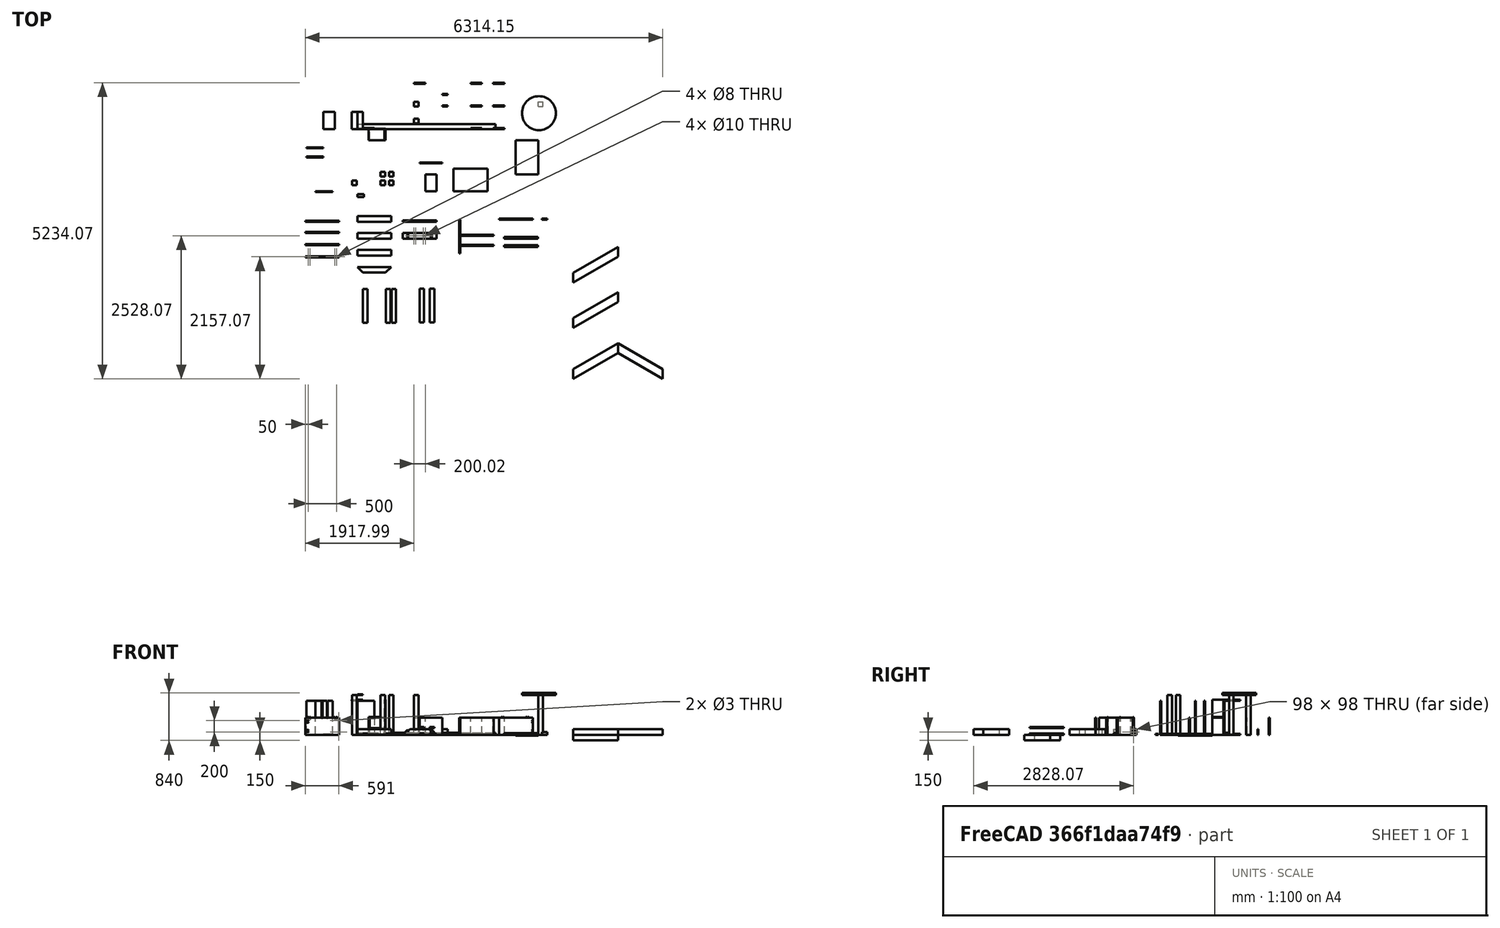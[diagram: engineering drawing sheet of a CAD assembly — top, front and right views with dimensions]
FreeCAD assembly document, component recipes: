
FREECAD ASSEMBLY — COMPONENT RECIPES ("Test001_features")

This assembly document has 25 components, labeled P0..P24 below (a component is one placed body or linked part). 18 of them carry a construction recipe — the FreeCAD feature program that regenerates the part from scratch, quoted from this document or its linked companion documents; the rest are supplied as boundary geometry only. No exploded tour is included for this assembly.
COMPONENT P0 — recipe-attached ("PDMirror Pad Body", modeled in this document).
Construction recipe (the document's own serialized feature program — sketch geometry with constraints, then the solid features built on it; lengths are millimeters unless a unit is written):

FEATURE [Sketcher::SketchObject] Sketch  label="Sketch001"
  AttachmentOffset = pos=(1300,-500,0) rot=(0,0,1;0rad)
  FullyConstrained = false
  MapMode = 5
  Placement = pos=(1300,-500,0) rot=(0,0,1;0rad)
  Support = -> [XY_Plane]
  sketch-geometry (4):
    g0: LineSegment StartX=0 StartY=-90.3636 StartZ=0 EndX=200 EndY=-90.3636 EndZ=0
    g1: LineSegment StartX=200 StartY=-90.3636 StartZ=0 EndX=200 EndY=-108.364 EndZ=0
    g2: LineSegment StartX=200 StartY=-108.364 StartZ=0 EndX=0 EndY=-108.364 EndZ=0
    g3: LineSegment StartX=0 StartY=-108.364 StartZ=0 EndX=0 EndY=-90.3636 EndZ=0
  constraints (11):
    c: Coincident(g0,g1)
    c: Coincident(g1,g2)
    c: Coincident(g2,g3)
    c: Coincident(g3,g0)
    c: Horizontal(g0)
    c: Horizontal(g2)
    c: Vertical(g1)
    c: Vertical(g3)
    c: DistanceX(g0,g0) = 200
    c: DistanceY(g3,g3) = 18
    c: DistanceX(g-1,g0) = 200
FEATURE [PartDesign::Pad] Pad  label="PDMirror Pad"
  AllowMultiFace = false
  Direction = (1,1,1)
  Length = 300
  Length2 = 100
  Profile = -> Sketch
  Type = 0
FEATURE [PartDesign::Mirrored] Mirrored
  BaseFeature = -> Pad
  MirrorPlane = -> Sketch [V_Axis]
  Originals = -> [Pad]
FEATURE [PartDesign::Body] Body  label="PDMirror Pad Body"
  Group = -> [Sketch,Pad,Mirrored]
  Origin = -> Origin
  Tip = -> Mirrored
COMPONENT P1 — recipe-attached ("Pad Single Body", modeled in this document).
Construction recipe (the document's own serialized feature program — sketch geometry with constraints, then the solid features built on it; lengths are millimeters unless a unit is written):

FEATURE [Sketcher::SketchObject] Sketch001  label="Sketch002"
  AttachmentOffset = pos=(1500,-1200,0) rot=(0,0,1;0rad)
  FullyConstrained = true
  MapMode = 5
  Placement = pos=(1500,-1200,0) rot=(0,0,1;0rad)
  Support = -> [XY_Plane001]
  sketch-geometry (4):
    g0: LineSegment StartX=-300 StartY=400 StartZ=0 EndX=-100 EndY=400 EndZ=0
    g1: LineSegment StartX=-100 StartY=400 StartZ=0 EndX=-100 EndY=100 EndZ=0
    g2: LineSegment StartX=-100 StartY=100 StartZ=0 EndX=-300 EndY=100 EndZ=0
    g3: LineSegment StartX=-300 StartY=100 StartZ=0 EndX=-300 EndY=400 EndZ=0
  constraints (12):
    c: Coincident(g0,g1)
    c: Coincident(g1,g2)
    c: Coincident(g2,g3)
    c: Coincident(g3,g0)
    c: Horizontal(g0)
    c: Horizontal(g2)
    c: Vertical(g1)
    c: Vertical(g3)
    c: DistanceX(g0,g0) = 200
    c: DistanceY(g3,g3) = 300
    c: DistanceY(g-1,g0) = 400
    c: DistanceX(g1,g-1) = 100
FEATURE [PartDesign::Pad] Pad001  label="Pad Single"
  AllowMultiFace = false
  Direction = (1,1,1)
  Length = 18
  Length2 = 100
  Profile = -> Sketch001
  Type = 0
FEATURE [PartDesign::Body] Body001  label="Pad Single Body"
  Group = -> [Sketch001,Pad001]
  Origin = -> Origin001
  Tip = -> Pad001
COMPONENT P2 — recipe-attached ("PDMulti 4 Pad Body", modeled in this document).
Construction recipe (the document's own serialized feature program — sketch geometry with constraints, then the solid features built on it; lengths are millimeters unless a unit is written):

FEATURE [Sketcher::SketchObject] Sketch002  label="Sketch003"
  AttachmentOffset = pos=(2000,-900,0) rot=(0,0,1;0rad)
  FullyConstrained = true
  MapMode = 5
  Placement = pos=(2000,-900,0) rot=(0,0,1;0rad)
  Support = -> [XY_Plane002]
  sketch-geometry (4):
    g0: LineSegment StartX=-300 StartY=200 StartZ=0 EndX=0 EndY=200 EndZ=0
    g1: LineSegment StartX=0 StartY=200 StartZ=0 EndX=0 EndY=0 EndZ=0
    g2: LineSegment StartX=0 StartY=0 StartZ=0 EndX=-300 EndY=0 EndZ=0
    g3: LineSegment StartX=-300 StartY=0 StartZ=0 EndX=-300 EndY=200 EndZ=0
  constraints (12):
    c: Coincident(g0,g1)
    c: Coincident(g1,g2)
    c: Coincident(g2,g3)
    c: Coincident(g3,g0)
    c: Horizontal(g0)
    c: Horizontal(g2)
    c: Vertical(g1)
    c: Vertical(g3)
    c: DistanceX(g0,g0) = 300
    c: DistanceY(g3,g3) = 200
    c: DistanceY(g1,g-1) = 0
    c: DistanceX(g1,g-1) = 0
FEATURE [PartDesign::Pad] Pad002  label="PDMulti 4 Pad"
  AllowMultiFace = false
  Direction = (1,1,1)
  Length = 18
  Length2 = 100
  Profile = -> Sketch002
  Type = 0
FEATURE [PartDesign::Mirrored] Mirrored001
  MirrorPlane = -> Sketch002 [V_Axis]
FEATURE [PartDesign::Mirrored] Mirrored002
  MirrorPlane = -> Sketch002 [H_Axis]
FEATURE [PartDesign::MultiTransform] MultiTransform
  BaseFeature = -> Pad002
  Originals = -> [Pad002]
  Transformations = -> [Mirrored001,Mirrored002]
FEATURE [PartDesign::Body] Body002  label="PDMulti 4 Pad Body"
  Group = -> [Sketch002,Pad002,MultiTransform,Mirrored001,Mirrored002]
  Origin = -> Origin002
  Tip = -> MultiTransform
COMPONENT P3 — recipe-attached ("PDMulti 8 Pad Body", modeled in this document).
Construction recipe (the document's own serialized feature program — sketch geometry with constraints, then the solid features built on it; lengths are millimeters unless a unit is written):

FEATURE [Sketcher::SketchObject] Sketch003  label="Sketch004"
  AttachmentOffset = pos=(3000,-500,0) rot=(0,0,1;0rad)
  FullyConstrained = true
  MapMode = 5
  Placement = pos=(3000,-500,0) rot=(0,0,1;0rad)
  Support = -> [XY_Plane003]
  sketch-geometry (4):
    g0: LineSegment StartX=-200 StartY=300 StartZ=0 EndX=0 EndY=300 EndZ=0
    g1: LineSegment StartX=0 StartY=300 StartZ=0 EndX=0 EndY=0 EndZ=0
    g2: LineSegment StartX=0 StartY=0 StartZ=0 EndX=-200 EndY=0 EndZ=0
    g3: LineSegment StartX=-200 StartY=0 StartZ=0 EndX=-200 EndY=300 EndZ=0
  constraints (11):
    c: Coincident(g0,g1)
    c: Coincident(g1,g2)
    c: Coincident(g2,g3)
    c: Coincident(g3,g0)
    c: Horizontal(g0)
    c: Horizontal(g2)
    c: Vertical(g1)
    c: Vertical(g3)
    c: Coincident(g1,g-1)
    c: DistanceX(g0,g0) = 200
    c: DistanceY(g3,g3) = 300
FEATURE [PartDesign::Pad] Pad003  label="PDMulti 8 Pad"
  AllowMultiFace = false
  Direction = (1,1,1)
  Length = 18
  Length2 = 100
  Profile = -> Sketch003
  Type = 0
FEATURE [PartDesign::Mirrored] Mirrored003
  MirrorPlane = -> Sketch003 [V_Axis]
FEATURE [PartDesign::Mirrored] Mirrored004
  MirrorPlane = -> Sketch003 [H_Axis]
FEATURE [PartDesign::Mirrored] Mirrored005
  MirrorPlane = -> XY_Plane003
FEATURE [PartDesign::MultiTransform] MultiTransform001
  BaseFeature = -> Pad003
  Originals = -> [Pad003]
  Transformations = -> [Mirrored003,Mirrored004,Mirrored005]
FEATURE [PartDesign::Body] Body003  label="PDMulti 8 Pad Body"
  Group = -> [Sketch003,Pad003,MultiTransform001,Mirrored003,Mirrored004,Mirrored005]
  Origin = -> Origin003
  Tip = -> MultiTransform001
COMPONENT P4 — recipe-attached ("Array Pad Body", modeled in this document).
Construction recipe (the document's own serialized feature program — sketch geometry with constraints, then the solid features built on it; lengths are millimeters unless a unit is written):

FEATURE [Sketcher::SketchObject] Sketch004  label="Sketch005"
  AttachmentOffset = pos=(500,-1000,0) rot=(0,0,1;0rad)
  FullyConstrained = true
  MapMode = 5
  Placement = pos=(500,-1000,0) rot=(0,0,1;0rad)
  Support = -> [XY_Plane004]
  sketch-geometry (4):
    g0: LineSegment StartX=-90 StartY=90 StartZ=0 EndX=-10 EndY=90 EndZ=0
    g1: LineSegment StartX=-10 StartY=90 StartZ=0 EndX=-10 EndY=10 EndZ=0
    g2: LineSegment StartX=-10 StartY=10 StartZ=0 EndX=-90 EndY=10 EndZ=0
    g3: LineSegment StartX=-90 StartY=10 StartZ=0 EndX=-90 EndY=90 EndZ=0
  constraints (12):
    c: Coincident(g0,g1)
    c: Coincident(g1,g2)
    c: Coincident(g2,g3)
    c: Coincident(g3,g0)
    c: Horizontal(g0)
    c: Horizontal(g2)
    c: Vertical(g1)
    c: Vertical(g3)
    c: DistanceY(g-1,g1) = 10
    c: DistanceX(g1,g-1) = 10
    c: DistanceX(g0,g0) = 80
    c: DistanceY(g3,g3) = 80
FEATURE [PartDesign::Pad] Pad004  label="Array Pad"
  AllowMultiFace = false
  Direction = (1,1,1)
  Length = 700
  Length2 = 100
  Profile = -> Sketch004
  Type = 0
FEATURE [PartDesign::Body] Body004  label="Array Pad Body"
  Group = -> [Sketch004,Pad004]
  Origin = -> Origin004
  Tip = -> Pad004
COMPONENT P5 — recipe-attached ("Array Polar Pad Body", modeled in this document).
Construction recipe (the document's own serialized feature program — sketch geometry with constraints, then the solid features built on it; lengths are millimeters unless a unit is written):

FEATURE [Sketcher::SketchObject] Sketch005  label="Sketch006"
  AttachmentOffset = pos=(0,-1000,0) rot=(0,0,1;0rad)
  FullyConstrained = true
  MapMode = 5
  Placement = pos=(0,-1000,0) rot=(0,0,1;0rad)
  Support = -> [XY_Plane005]
  sketch-geometry (4):
    g0: LineSegment StartX=-90 StartY=90 StartZ=0 EndX=-10 EndY=90 EndZ=0
    g1: LineSegment StartX=-10 StartY=90 StartZ=0 EndX=-10 EndY=10 EndZ=0
    g2: LineSegment StartX=-10 StartY=10 StartZ=0 EndX=-90 EndY=10 EndZ=0
    g3: LineSegment StartX=-90 StartY=10 StartZ=0 EndX=-90 EndY=90 EndZ=0
  constraints (12):
    c: Coincident(g0,g1)
    c: Coincident(g1,g2)
    c: Coincident(g2,g3)
    c: Coincident(g3,g0)
    c: Horizontal(g0)
    c: Horizontal(g2)
    c: Vertical(g1)
    c: Vertical(g3)
    c: DistanceY(g-1,g1) = 10
    c: DistanceX(g1,g-1) = 10
    c: DistanceX(g0,g0) = 80
    c: DistanceY(g3,g3) = 80
FEATURE [PartDesign::Pad] Pad005  label="Array Polar Pad"
  AllowMultiFace = false
  Direction = (1,1,1)
  Length = 700
  Length2 = 100
  Profile = -> Sketch005
  Type = 0
FEATURE [PartDesign::Body] Body005  label="Array Polar Pad Body"
  Group = -> [Sketch005,Pad005]
  Origin = -> Origin005
  Tip = -> Pad005
COMPONENT P6 — recipe-attached ("Table Top Parent Body", modeled in this document).
Construction recipe (the document's own serialized feature program — sketch geometry with constraints, then the solid features built on it; lengths are millimeters unless a unit is written):

FEATURE [Sketcher::SketchObject] Sketch006  label="Sketch007"
  AttachmentOffset = pos=(0,0,700) rot=(0,0,1;0rad)
  FullyConstrained = false
  MapMode = 5
  Placement = pos=(0,0,700) rot=(0,0,1;0rad)
  Support = -> [XY_Plane006]
  sketch-geometry (1):
    g0: Circle CenterX=3208.45 CenterY=279.77 CenterZ=0 NormalX=0 NormalY=0 NormalZ=1 AngleXU=0 Radius=300
  constraints (1):
    c: Radius(g0) = 300  'This is my round table top radius'
FEATURE [PartDesign::Pad] Pad006  label="Table Top"
  Direction = (1,1,1)
  Length = 40
  Length2 = 100
  Profile = -> Sketch006
  Type = 0
FEATURE [PartDesign::Body] Body006  label="Table Top Parent Body"
  Group = -> [Sketch006,Pad006]
  Origin = -> Origin006
  Tip = -> Pad006
COMPONENT P7 — recipe-attached ("Screw, Body", modeled in this document).
Construction recipe (the document's own serialized feature program — sketch geometry with constraints, then the solid features built on it; lengths are millimeters unless a unit is written):

FEATURE [Sketcher::SketchObject] Sketch007  label="Core, Pattern"
  FullyConstrained = true
  MapMode = 5
  Placement = pos=(0,0,0) rot=(1,0,0;1.5708rad)
  Support = -> [XZ_Plane007]
  expr: Constraints[10] = Spreadsheet.corer
  expr: Constraints[11] = 2 * Spreadsheet.tjump
  expr: Constraints[12] = Spreadsheet.sheight
  expr: Constraints[13] = Spreadsheet.hheight1
  expr: Constraints[14] = Spreadsheet.hheight2
  expr: Constraints[15] = Spreadsheet.hr
  expr: Constraints[16] = Spreadsheet.hheight1
  sketch-geometry (6):
    g0: LineSegment StartX=0 StartY=0 StartZ=0 EndX=1.5 EndY=3.8 EndZ=0
    g1: LineSegment StartX=1.5 StartY=3.8 StartZ=0 EndX=1.5 EndY=37 EndZ=0
    g2: LineSegment StartX=1.5 StartY=37 StartZ=0 EndX=2 EndY=37.5 EndZ=0
    g3: LineSegment StartX=2 StartY=37.5 StartZ=0 EndX=3.87 EndY=40 EndZ=0
    g4: LineSegment StartX=3.87 StartY=40 StartZ=0 EndX=0 EndY=40 EndZ=0
    g5: LineSegment StartX=0 StartY=40 StartZ=0 EndX=0 EndY=0 EndZ=0
  constraints (17):
    c: Coincident(g-1,g0)
    c: Coincident(g0,g1)
    c: Vertical(g1)
    c: Coincident(g1,g2)
    c: Coincident(g2,g3)
    c: Coincident(g3,g4)
    c: PointOnObject(g4,g-2)
    c: Horizontal(g4)
    c: Coincident(g4,g5)
    c: Coincident(g5,g0)
    c: DistanceX(g0,g0) = 1.5
    c: DistanceY(g0,g0) = 3.8
    c: DistanceY(g5,g5) = 40
    c: DistanceY(g1,g2) = 0.5
    c: DistanceY(g2,g3) = 2.5
    c: DistanceX(g4,g3) = 3.87
    c: DistanceX(g1,g2) = 0.5
FEATURE [PartDesign::Revolution] Revolution  label="Core"
  Angle = 360
  Axis = (0,-2e-16,1)
  Base = (0,0,0)
  Placement = pos=(0,0,0) rot=(1,0,0;1.5708rad)
  Profile = -> Sketch007
  ReferenceAxis = -> Sketch007 [V_Axis]
  Reversed = true
FEATURE [Sketcher::SketchObject] Sketch008  label="Thread, Pattern"
  FullyConstrained = true
  MapMode = 5
  Placement = pos=(0,0,0) rot=(1,0,0;1.5708rad)
  Support = -> [XZ_Plane007]
  expr: Constraints[2] = Spreadsheet.spikesize
  expr: Constraints[3] = Spreadsheet.corer
  sketch-geometry (3):
    g0: LineSegment StartX=1.5 StartY=3.675 StartZ=0 EndX=2 EndY=3.8 EndZ=0
    g1: LineSegment StartX=2 StartY=3.8 StartZ=0 EndX=1.5 EndY=3.925 EndZ=0
    g2: LineSegment StartX=1.5 StartY=3.925 StartZ=0 EndX=1.5 EndY=3.675 EndZ=0
  constraints (9):
    c: Coincident(g0,g1)
    c: Equal(g0,g1)
    c: DistanceY(g-1,g0) = 3.8
    c: DistanceX(g-1,g0) = 1.5
    c: DistanceX(g0,g0) = 0.5
    c: DistanceY(g0,g1) = 0.25
    c: Vertical(g1,g0)
    c: Coincident(g2,g1)
    c: Coincident(g2,g0)
FEATURE [PartDesign::AdditiveHelix] AdditiveHelix  label="Thread, Core"
  Angle = 0
  Axis = (0,-2e-16,1)
  Base = (0,0,0)
  BaseFeature = -> Revolution
  Growth = 0
  HasBeenEdited = true
  Height = 20.4
  LeftHanded = false
  Mode = 0
  Outside = false
  Pitch = 1.9
  Placement = pos=(0,0,0) rot=(1,0,0;1.5708rad)
  Profile = -> Sketch008
  ReferenceAxis = -> Sketch008 [V_Axis]
  Turns = 10.7368
  expr: Height = Spreadsheet.theight - Spreadsheet.spikesize
  expr: Pitch = Spreadsheet.tjump
FEATURE [PartDesign::AdditiveHelix] AdditiveHelix001  label="Thread, Spike"
  Angle = -30
  Axis = (0,-2e-16,1)
  Base = (0,0,0)
  BaseFeature = -> AdditiveHelix
  Growth = -1.09697
  HasBeenEdited = true
  Height = 2.53333
  LeftHanded = false
  Mode = 0
  Outside = false
  Pitch = 1.9
  Placement = pos=(0,0,0) rot=(1,0,0;1.5708rad)
  Profile = -> Sketch008
  ReferenceAxis = -> Sketch008 [V_Axis]
  Reversed = true
  Turns = 1.33333
  expr: Height = 2 * Spreadsheet.spikesize / 3
  expr: Pitch = Spreadsheet.tjump
FEATURE [Sketcher::SketchObject] Sketch009  label="Bit, Pattern 1"
  FullyConstrained = true
  MapMode = 5
  Placement = pos=(0,0,0) rot=(0.57735,0.57735,0.57735;2.0944rad)
  Support = -> [YZ_Plane007]
  expr: Constraints[16] = Spreadsheet.hheight2 / 4
  expr: Constraints[6] = Spreadsheet.coredia
  expr: Constraints[7] = Spreadsheet.sheight
  expr: Constraints[8] = Spreadsheet.bitsize
  expr: Constraints[9] = Spreadsheet.hheight2 / 2
  sketch-geometry (6):
    g0: LineSegment StartX=-2.13 StartY=40 StartZ=0 EndX=2.13 EndY=40 EndZ=0
    g1: LineSegment StartX=2.13 StartY=40 StartZ=0 EndX=1.5 EndY=38.75 EndZ=0
    g2: LineSegment StartX=1.5 StartY=38.75 StartZ=0 EndX=0.875 EndY=38.75 EndZ=0
    g3: LineSegment StartX=-1.5 StartY=38.75 StartZ=0 EndX=-2.13 EndY=40 EndZ=0
    g4: ArcOfCircle CenterX=0 CenterY=40 CenterZ=0 NormalX=0 NormalY=0 NormalZ=1 AngleXU=0 Radius=1.52582 StartAngle=4.10166 EndAngle=5.32311
    g5: LineSegment StartX=-0.875 StartY=38.75 StartZ=0 EndX=-1.5 EndY=38.75 EndZ=0
  constraints (17):
    c: Coincident(g0,g1)
    c: Coincident(g1,g2)
    c: Coincident(g5,g3)
    c: Coincident(g3,g0)
    c: Symmetric(g1,g5,g-2)
    c: Symmetric(g0,g0,g-2)
    c: DistanceX(g5,g2) = 3
    c: DistanceY(g-1,g0) = 40
    c: DistanceX(g0,g0) = 4.26
    c: DistanceY(g1,g0) = 1.25
    c: Horizontal(g4,g0)
    c: PointOnObject(g4,g-2)
    c: Coincident(g2,g4)
    c: Coincident(g5,g4)
    c: Horizontal(g3,g4)
    c: Horizontal(g4,g2)
    c: DistanceX(g2,g1) = 0.625
FEATURE [PartDesign::Pocket] Pocket  label="Bit, Pocket 1"
  BaseFeature = -> AdditiveHelix001
  Direction = (-1,2e-16,-3e-16)
  Length = 1
  Length2 = 5
  Midplane = true
  Placement = pos=(0,0,0) rot=(1,0,0;1.5708rad)
  Profile = -> Sketch009
  ReferenceAxis = -> Sketch009 [N_Axis]
  Type = 0
FEATURE [Sketcher::SketchObject] Sketch010  label="Bit, Line, Pattern 1"
  AttachmentOffset = pos=(0,0,0) rot=(0,1,0;0.785398rad)
  FullyConstrained = true
  MapMode = 5
  Placement = pos=(0,0,0) rot=(0.281085,0.678598,0.678598;2.59356rad)
  Support = -> [YZ_Plane007]
  expr: Constraints[10] = Spreadsheet.sheight
  expr: Constraints[6] = Spreadsheet.bitsize
  sketch-geometry (4):
    g0: LineSegment StartX=2.13 StartY=40 StartZ=0 EndX=2.13 EndY=39.9 EndZ=0
    g1: LineSegment StartX=2.13 StartY=39.9 StartZ=0 EndX=-2.13 EndY=39.9 EndZ=0
    g2: LineSegment StartX=-2.13 StartY=39.9 StartZ=0 EndX=-2.13 EndY=40 EndZ=0
    g3: LineSegment StartX=-2.13 StartY=40 StartZ=0 EndX=2.13 EndY=40 EndZ=0
  constraints (11):
    c: Coincident(g0,g1)
    c: Coincident(g1,g2)
    c: Coincident(g3,g2)
    c: Coincident(g3,g0)
    c: Equal(g1,g3)
    c: Equal(g0,g2)
    c: DistanceX(g3,g3) = 4.26
    c: Vertical(g2)
    c: Symmetric(g1,g0,g-2)
    c: DistanceY(g0,g0) = 0.1
    c: DistanceY(g-1,g0) = 40
FEATURE [PartDesign::Pocket] Pocket001  label="Bit, Lines 1"
  BaseFeature = -> Pocket
  Direction = (-0.707107,-0.707107,1e-16)
  Length = 0.1
  Length2 = 5
  Midplane = true
  Placement = pos=(0,0,0) rot=(1,0,0;1.5708rad)
  Profile = -> Sketch010
  ReferenceAxis = -> Sketch010 [N_Axis]
  Type = 0
FEATURE [PartDesign::PolarPattern] PolarPattern  label="Bit, PolarPattern"
  Angle = 90
  Axis = -> Sketch010 [V_Axis]
  BaseFeature = -> Pocket001
  Occurrences = 2
  Originals = -> [Pocket001,Pocket]
  Placement = pos=(0,0,0) rot=(1,0,0;1.5708rad)
FEATURE [Sketcher::SketchObject] Sketch011  label="Thread, Top, Pattern"
  FullyConstrained = true
  MapMode = 5
  Placement = pos=(0,0,0) rot=(1,0,0;1.5708rad)
  Support = -> [XZ_Plane007]
  expr: Constraints[2] = Spreadsheet.tjump
  expr: Constraints[4] = Spreadsheet.corer
  expr: Constraints[5] = Spreadsheet.theight
  sketch-geometry (4):
    g0: LineSegment StartX=1.5 StartY=26.1 StartZ=0 EndX=1.5 EndY=24.2 EndZ=0
    g1: LineSegment StartX=1.5 StartY=24.2 StartZ=0 EndX=2.5 EndY=24.2 EndZ=0
    g2: LineSegment StartX=1.5 StartY=26.1 StartZ=0 EndX=2.5 EndY=26.1 EndZ=0
    g3: LineSegment StartX=2.5 StartY=26.1 StartZ=0 EndX=2.5 EndY=24.2 EndZ=0
  constraints (12):
    c: Vertical(g0)
    c: Coincident(g0,g1)
    c: DistanceY(g0,g0) = 1.9
    c: DistanceX(g0,g1) = 1
    c: DistanceX(g-1,g0) = 1.5
    c: DistanceY(g-1,g1) = 24.2
    c: Coincident(g0,g2)
    c: Coincident(g2,g3)
    c: Coincident(g3,g1)
    c: Horizontal(g2)
    c: Vertical(g3)
    c: Horizontal(g1)
FEATURE [PartDesign::SubtractiveHelix] SubtractiveHelix  label="Thread, Top"
  Angle = 15
  Axis = (0,-2e-16,1)
  Base = (0,0,0)
  BaseFeature = -> PolarPattern
  Growth = 0.509103
  HasBeenEdited = true
  Height = 1.9
  LeftHanded = false
  Mode = 0
  Outside = false
  Pitch = 1.9
  Placement = pos=(0,0,0) rot=(1,0,0;1.5708rad)
  Profile = -> Sketch011
  ReferenceAxis = -> Sketch011 [V_Axis]
  Reversed = true
  Turns = 1
  expr: Height = Spreadsheet.tjump
  expr: Pitch = Spreadsheet.tjump
FEATURE [PartDesign::Body] Body007  label="Screw, Body"
  Group = -> [Sketch007,Revolution,Sketch008,AdditiveHelix,AdditiveHelix001,Sketch009,Pocket,Sketch010,Pocket001,PolarPattern,Sketch011,SubtractiveHelix]
  Origin = -> Origin007
  Tip = -> SubtractiveHelix
COMPONENT P8 — geometry summary ("Link"; no construction recipe available for this part):
  bounding box: 600.0 x 300.0 x 180.0 mm
  tessellated surface: 24 triangles
  volume: 6480000 mm^3 (20% of its bounding box)
  symmetry: 2-fold rotationally symmetric about the x axis; 2-fold rotationally symmetric about the y axis; 2-fold rotationally symmetric about the z axis; mirror-symmetric across its x mid-plane, y mid-plane, z mid-plane
COMPONENT P9 — geometry summary ("Link, Cut"; no construction recipe available for this part):
  bounding box: 600.0 x 300.0 x 18.0 mm
  tessellated surface: 44 triangles
  volume: 3037824 mm^3 (94% of its bounding box)
  symmetry: mirror-symmetric across its y mid-plane
COMPONENT P10 — geometry summary ("Link, nested 1 link "; no construction recipe available for this part):
  bounding box: 600.0 x 180.0 x 20.0 mm
  tessellated surface: 24 triangles
  volume: 1920000 mm^3 (89% of its bounding box)
  symmetry: 2-fold rotationally symmetric about the x axis; 2-fold rotationally symmetric about the y axis; 2-fold rotationally symmetric about the z axis; mirror-symmetric across its x mid-plane, y mid-plane, z mid-plane
COMPONENT P11 — geometry summary ("Link, nested 2 link"; no construction recipe available for this part):
  bounding box: 600.0 x 180.0 x 20.0 mm
  tessellated surface: 24 triangles
  volume: 1920000 mm^3 (89% of its bounding box)
  symmetry: 2-fold rotationally symmetric about the x axis; 2-fold rotationally symmetric about the y axis; 2-fold rotationally symmetric about the z axis; mirror-symmetric across its x mid-plane, y mid-plane, z mid-plane
COMPONENT P12 — recipe-attached ("Link, panelZX002 ", modeled in this document).
Construction recipe (the document's own serialized feature program — sketch geometry with constraints, then the solid features built on it; lengths are millimeters unless a unit is written):

FEATURE [Sketcher::SketchObject] Sketch035  label="Pattern, panel2pad001"
  FullyConstrained = true
  MapMode = 5
  Placement = pos=(0,0,0) rot=(1,0,0;1.5708rad)
  Support = -> [XZ_Plane025]
  sketch-geometry (4):
    g0: LineSegment StartX=0 StartY=600 StartZ=0 EndX=300 EndY=600 EndZ=0
    g1: LineSegment StartX=300 StartY=600 StartZ=0 EndX=300 EndY=0 EndZ=0
    g2: LineSegment StartX=300 StartY=0 StartZ=0 EndX=0 EndY=0 EndZ=0
    g3: LineSegment StartX=0 StartY=0 StartZ=0 EndX=0 EndY=600 EndZ=0
  constraints (11):
    c: Coincident(g0,g1)
    c: Coincident(g1,g2)
    c: Coincident(g2,g3)
    c: Coincident(g3,g0)
    c: Horizontal(g0)
    c: Horizontal(g2)
    c: Vertical(g1)
    c: Vertical(g3)
    c: Coincident(g2,g-1)
    c: DistanceX(g0,g0) = 300  'SizeX'
    c: DistanceY(g3,g3) = 600  'SizeY'
FEATURE [PartDesign::Pad] Pad015  label="panel2pad"
  Direction = (0,-1,2e-16)
  Length = 18
  Length2 = 10
  Placement = pos=(0,0,0) rot=(1,0,0;1.5708rad)
  Profile = -> Sketch035
  Reversed = true
  Type = 0
FEATURE [Sketcher::SketchObject] routerPattern002
  FullyConstrained = true
  Placement = pos=(150,1.332e-13,600) rot=(0,1,0;1.5708rad)
  sketch-geometry (4):
    g0: ArcOfCircle CenterX=18 CenterY=-18 CenterZ=0 NormalX=0 NormalY=0 NormalZ=1 AngleXU=0 Radius=18 StartAngle=1.5708 EndAngle=3.14159
    g1: ArcOfCircle CenterX=-18 CenterY=18 CenterZ=0 NormalX=0 NormalY=0 NormalZ=1 AngleXU=0 Radius=18 StartAngle=4.71239 EndAngle=6.28319
    g2: ArcOfCircle CenterX=18 CenterY=18 CenterZ=0 NormalX=0 NormalY=0 NormalZ=1 AngleXU=0 Radius=18 StartAngle=3.14159 EndAngle=4.71239
    g3: ArcOfCircle CenterX=-18 CenterY=-18 CenterZ=0 NormalX=0 NormalY=0 NormalZ=1 AngleXU=0 Radius=18 StartAngle=6.28318 EndAngle=7.85398
  constraints (16):
    c: Equal(g3,g1)
    c: Equal(g1,g2)
    c: Equal(g2,g0)
    c: Vertical(g0,g2)
    c: Horizontal(g3,g0)
    c: Vertical(g1,g3)
    c: Horizontal(g1,g2)
    c: Coincident(g1,g2)
    c: Coincident(g0,g2)
    c: Coincident(g3,g0)
    c: Coincident(g3,g1)
    c: PointOnObject(g1,g-1)
    c: PointOnObject(g1,g-2)
    c: DistanceY(g0,g-1) = 18
    c: Vertical(g0,g0)
    c: Horizontal(g1,g1)
FEATURE [PartDesign::Pocket] router002  label="RoundOver "
  BaseFeature = -> Pad015
  Direction = (-1,0,-2e-16)
  Length = 5
  Length2 = 5
  Midplane = true
  Placement = pos=(0,0,0) rot=(1,0,0;1.5708rad)
  Profile = -> routerPattern002
  Type = 1
FEATURE [Sketcher::SketchObject] routerPattern003
  FullyConstrained = true
  Placement = pos=(300,6.7e-14,300) rot=(0,0,1;0rad)
  sketch-geometry (4):
    g0: ArcOfCircle CenterX=18 CenterY=-18 CenterZ=0 NormalX=0 NormalY=0 NormalZ=1 AngleXU=0 Radius=18 StartAngle=1.5708 EndAngle=3.14159
    g1: ArcOfCircle CenterX=-18 CenterY=18 CenterZ=0 NormalX=0 NormalY=0 NormalZ=1 AngleXU=0 Radius=18 StartAngle=4.71239 EndAngle=6.28319
    g2: ArcOfCircle CenterX=18 CenterY=18 CenterZ=0 NormalX=0 NormalY=0 NormalZ=1 AngleXU=0 Radius=18 StartAngle=3.14159 EndAngle=4.71239
    g3: ArcOfCircle CenterX=-18 CenterY=-18 CenterZ=0 NormalX=0 NormalY=0 NormalZ=1 AngleXU=0 Radius=18 StartAngle=6.28318 EndAngle=7.85398
  constraints (16):
    c: Equal(g3,g1)
    c: Equal(g1,g2)
    c: Equal(g2,g0)
    c: Vertical(g0,g2)
    c: Horizontal(g3,g0)
    c: Vertical(g1,g3)
    c: Horizontal(g1,g2)
    c: Coincident(g1,g2)
    c: Coincident(g0,g2)
    c: Coincident(g3,g0)
    c: Coincident(g3,g1)
    c: PointOnObject(g1,g-1)
    c: PointOnObject(g1,g-2)
    c: DistanceY(g0,g-1) = 18
    c: Vertical(g0,g0)
    c: Horizontal(g1,g1)
FEATURE [PartDesign::Pocket] router003  label="RoundOver 001"
  BaseFeature = -> router002
  Direction = (0,0,-1)
  Length = 5
  Length2 = 5
  Midplane = true
  Placement = pos=(0,0,0) rot=(1,0,0;1.5708rad)
  Profile = -> routerPattern003
  Type = 1
FEATURE [Sketcher::SketchObject] routerPattern004
  FullyConstrained = true
  Placement = pos=(150,0,0) rot=(0,1,0;1.5708rad)
  sketch-geometry (4):
    g0: ArcOfCircle CenterX=18 CenterY=-18 CenterZ=0 NormalX=0 NormalY=0 NormalZ=1 AngleXU=0 Radius=18 StartAngle=1.5708 EndAngle=3.14159
    g1: ArcOfCircle CenterX=-18 CenterY=18 CenterZ=0 NormalX=0 NormalY=0 NormalZ=1 AngleXU=0 Radius=18 StartAngle=4.71239 EndAngle=6.28319
    g2: ArcOfCircle CenterX=18 CenterY=18 CenterZ=0 NormalX=0 NormalY=0 NormalZ=1 AngleXU=0 Radius=18 StartAngle=3.14159 EndAngle=4.71239
    g3: ArcOfCircle CenterX=-18 CenterY=-18 CenterZ=0 NormalX=0 NormalY=0 NormalZ=1 AngleXU=0 Radius=18 StartAngle=1.97117e-06 EndAngle=1.5708
  constraints (16):
    c: Equal(g3,g1)
    c: Equal(g1,g2)
    c: Equal(g2,g0)
    c: Vertical(g0,g2)
    c: Horizontal(g3,g0)
    c: Vertical(g1,g3)
    c: Horizontal(g1,g2)
    c: Coincident(g1,g2)
    c: Coincident(g0,g2)
    c: Coincident(g3,g0)
    c: Coincident(g3,g1)
    c: PointOnObject(g1,g-1)
    c: PointOnObject(g1,g-2)
    c: DistanceY(g0,g-1) = 18
    c: Vertical(g0,g0)
    c: Horizontal(g1,g1)
FEATURE [PartDesign::Pocket] router004  label="RoundOver 002"
  BaseFeature = -> router003
  Direction = (-1,0,-2e-16)
  Length = 5
  Length2 = 5
  Midplane = true
  Placement = pos=(0,0,0) rot=(1,0,0;1.5708rad)
  Profile = -> routerPattern004
  Type = 1
FEATURE [Sketcher::SketchObject] routerPattern005
  FullyConstrained = true
  Placement = pos=(0,6.7e-14,300) rot=(0,0,1;0rad)
  sketch-geometry (4):
    g0: ArcOfCircle CenterX=18 CenterY=-18 CenterZ=0 NormalX=0 NormalY=0 NormalZ=1 AngleXU=0 Radius=18 StartAngle=1.5708 EndAngle=3.14159
    g1: ArcOfCircle CenterX=-18 CenterY=18 CenterZ=0 NormalX=0 NormalY=0 NormalZ=1 AngleXU=0 Radius=18 StartAngle=4.71239 EndAngle=6.28319
    g2: ArcOfCircle CenterX=18 CenterY=18 CenterZ=0 NormalX=0 NormalY=0 NormalZ=1 AngleXU=0 Radius=18 StartAngle=3.14159 EndAngle=4.71239
    g3: ArcOfCircle CenterX=-18 CenterY=-18 CenterZ=0 NormalX=0 NormalY=0 NormalZ=1 AngleXU=0 Radius=18 StartAngle=6.28318 EndAngle=7.85398
  constraints (16):
    c: Equal(g3,g1)
    c: Equal(g1,g2)
    c: Equal(g2,g0)
    c: Vertical(g0,g2)
    c: Horizontal(g3,g0)
    c: Vertical(g1,g3)
    c: Horizontal(g1,g2)
    c: Coincident(g1,g2)
    c: Coincident(g0,g2)
    c: Coincident(g3,g0)
    c: Coincident(g3,g1)
    c: PointOnObject(g1,g-1)
    c: PointOnObject(g1,g-2)
    c: DistanceY(g0,g-1) = 18
    c: Vertical(g0,g0)
    c: Horizontal(g1,g1)
FEATURE [PartDesign::Pocket] router005  label="RoundOver 003"
  BaseFeature = -> router004
  Direction = (0,0,-1)
  Length = 5
  Length2 = 5
  Midplane = true
  Placement = pos=(0,0,0) rot=(1,0,0;1.5708rad)
  Profile = -> routerPattern005
  Type = 1
FEATURE [PartDesign::Body] Body016  label="Body, panel2pad001"
  Group = -> [Sketch035,Pad015,routerPattern002,router002,routerPattern003,router003,routerPattern004,router004,routerPattern005,router005]
  Origin = -> Origin025
  Tip = -> router005
COMPONENT P13 — same part as P12; its construction recipe is shown at P12.
COMPONENT P14 — geometry summary ("Link, Screw 4 x 40 mm "; no construction recipe available for this part):
  bounding box: 40.0 x 7.7 x 7.4 mm
  tessellated surface: 492 triangles
  volume: 317 mm^3 (14% of its bounding box)
COMPONENT P15 — geometry summary ("Link, Screw 4 x 40 mm 001"; no construction recipe available for this part):
  bounding box: 40.0 x 7.7 x 7.4 mm
  tessellated surface: 492 triangles
  volume: 317 mm^3 (14% of its bounding box)
COMPONENT P16 — recipe-attached ("Part, Construction", modeled in this document).
Construction recipe (the document's own serialized feature program — sketch geometry with constraints, then the solid features built on it; lengths are millimeters unless a unit is written):

FEATURE [Sketcher::SketchObject] Sketch012  label="Pattern, Construction"
  AttachmentOffset = pos=(0,-1638,0) rot=(0,0,1;0rad)
  FullyConstrained = true
  MapMode = 5
  Placement = pos=(0,-1638,0) rot=(0,0,1;0rad)
  Support = -> [XY_Plane009]
  sketch-geometry (4):
    g0: LineSegment StartX=0 StartY=100 StartZ=0 EndX=600 EndY=100 EndZ=0
    g1: LineSegment StartX=600 StartY=100 StartZ=0 EndX=600 EndY=0 EndZ=0
    g2: LineSegment StartX=600 StartY=0 StartZ=0 EndX=0 EndY=0 EndZ=0
    g3: LineSegment StartX=0 StartY=0 StartZ=0 EndX=0 EndY=100 EndZ=0
  constraints (11):
    c: Coincident(g0,g1)
    c: Coincident(g1,g2)
    c: Coincident(g2,g3)
    c: Coincident(g3,g0)
    c: Horizontal(g0)
    c: Horizontal(g2)
    c: Vertical(g1)
    c: Vertical(g3)
    c: Coincident(g2,g-1)
    c: DistanceX(g0,g0) = 600  'SizeX'
    c: DistanceY(g3,g3) = 100  'SizeY'
FEATURE [PartDesign::Pad] Pad007  label="Profile Simple"
  Direction = (0,0,1)
  Length = 100
  Length2 = 10
  Profile = -> Sketch012
  Type = 0
FEATURE [PartDesign::Thickness] Profile
  Base = -> Pad007 [Face2,Face4]
  BaseFeature = -> Pad007
  Intersection = false
  Join = 0
  Mode = 0
  Reversed = true
  SupportTransform = false
  Value = 1
FEATURE [PartDesign::Body] Body008  label="Body, Construction"
  Group = -> [Sketch012,Pad007,Profile]
  Origin = -> Origin009
  Tip = -> Profile
COMPONENT P17 — recipe-attached ("Part, Construction001", modeled in this document).
Construction recipe (the document's own serialized feature program — sketch geometry with constraints, then the solid features built on it; lengths are millimeters unless a unit is written):

FEATURE [Sketcher::SketchObject] Sketch013  label="Pattern, Construction001"
  AttachmentOffset = pos=(0,-1938,0) rot=(0,0,1;0rad)
  FullyConstrained = true
  MapMode = 5
  Placement = pos=(0,-1938,0) rot=(0,0,1;0rad)
  Support = -> [XY_Plane011]
  sketch-geometry (4):
    g0: LineSegment StartX=0 StartY=100 StartZ=0 EndX=600 EndY=100 EndZ=0
    g1: LineSegment StartX=600 StartY=100 StartZ=0 EndX=600 EndY=0 EndZ=0
    g2: LineSegment StartX=600 StartY=0 StartZ=0 EndX=0 EndY=0 EndZ=0
    g3: LineSegment StartX=0 StartY=0 StartZ=0 EndX=0 EndY=100 EndZ=0
  constraints (11):
    c: Coincident(g0,g1)
    c: Coincident(g1,g2)
    c: Coincident(g2,g3)
    c: Coincident(g3,g0)
    c: Horizontal(g0)
    c: Horizontal(g2)
    c: Vertical(g1)
    c: Vertical(g3)
    c: Coincident(g2,g-1)
    c: DistanceX(g0,g0) = 600  'SizeX'
    c: DistanceY(g3,g3) = 100  'SizeY'
FEATURE [PartDesign::Pad] Pad008  label="Profile Angle 1"
  Direction = (0,0,1)
  Length = 100
  Length2 = 10
  Profile = -> Sketch013
  Type = 0
FEATURE [PartDesign::Thickness] Angle
  Base = -> Pad008 [Face2,Face4,Face6]
  BaseFeature = -> Pad008
  Intersection = false
  Join = 0
  Mode = 0
  Reversed = true
  SupportTransform = false
  Value = 1
FEATURE [PartDesign::Body] Body009  label="Body, Construction001"
  Group = -> [Sketch013,Pad008,Angle]
  Origin = -> Origin011
  Tip = -> Angle
COMPONENT P18 — recipe-attached ("Part, Construction002", modeled in this document).
Construction recipe (the document's own serialized feature program — sketch geometry with constraints, then the solid features built on it; lengths are millimeters unless a unit is written):

FEATURE [Sketcher::SketchObject] Sketch014  label="Pattern, Construction002"
  AttachmentOffset = pos=(0,-2238,0) rot=(0,0,1;0rad)
  FullyConstrained = true
  MapMode = 5
  Placement = pos=(0,-2238,0) rot=(0,0,1;0rad)
  Support = -> [XY_Plane013]
  sketch-geometry (4):
    g0: LineSegment StartX=0 StartY=100 StartZ=0 EndX=600 EndY=100 EndZ=0
    g1: LineSegment StartX=600 StartY=100 StartZ=0 EndX=600 EndY=0 EndZ=0
    g2: LineSegment StartX=600 StartY=0 StartZ=0 EndX=0 EndY=0 EndZ=0
    g3: LineSegment StartX=0 StartY=0 StartZ=0 EndX=0 EndY=100 EndZ=0
  constraints (11):
    c: Coincident(g0,g1)
    c: Coincident(g1,g2)
    c: Coincident(g2,g3)
    c: Coincident(g3,g0)
    c: Horizontal(g0)
    c: Horizontal(g2)
    c: Vertical(g1)
    c: Vertical(g3)
    c: Coincident(g2,g-1)
    c: DistanceX(g0,g0) = 600  'SizeX'
    c: DistanceY(g3,g3) = 100  'SizeY'
FEATURE [PartDesign::Pad] Pad009  label="Profile Angle 2"
  Direction = (0,0,1)
  Length = 100
  Length2 = 10
  Profile = -> Sketch014
  Type = 0
FEATURE [PartDesign::Thickness] Angle001
  Base = -> Pad009 [Face2,Face4,Face3,Face6]
  BaseFeature = -> Pad009
  Intersection = false
  Join = 0
  Mode = 0
  Reversed = true
  SupportTransform = false
  Value = 1
FEATURE [PartDesign::Body] Body010  label="Body, Construction002"
  Group = -> [Sketch014,Pad009,Angle001]
  Origin = -> Origin013
  Tip = -> Angle001
COMPONENT P19 — recipe-attached ("Part, Construction003", modeled in this document).
Construction recipe (the document's own serialized feature program — sketch geometry with constraints, then the solid features built on it; lengths are millimeters unless a unit is written):

FEATURE [Sketcher::SketchObject] Sketch015  label="Pattern, Construction003"
  AttachmentOffset = pos=(0,-2538,0) rot=(0,0,1;0rad)
  FullyConstrained = true
  MapMode = 5
  Placement = pos=(0,-2538,0) rot=(0,0,1;0rad)
  Support = -> [XY_Plane015]
  sketch-geometry (4):
    g0: LineSegment StartX=0 StartY=100 StartZ=0 EndX=600 EndY=100 EndZ=0
    g1: LineSegment StartX=600 StartY=100 StartZ=0 EndX=600 EndY=0 EndZ=0
    g2: LineSegment StartX=600 StartY=0 StartZ=0 EndX=0 EndY=0 EndZ=0
    g3: LineSegment StartX=0 StartY=0 StartZ=0 EndX=0 EndY=100 EndZ=0
  constraints (11):
    c: Coincident(g0,g1)
    c: Coincident(g1,g2)
    c: Coincident(g2,g3)
    c: Coincident(g3,g0)
    c: Horizontal(g0)
    c: Horizontal(g2)
    c: Vertical(g1)
    c: Vertical(g3)
    c: Coincident(g2,g-1)
    c: DistanceX(g0,g0) = 600  'SizeX'
    c: DistanceY(g3,g3) = 100  'SizeY'
FEATURE [PartDesign::Pad] Pad010  label="Profile Angle 45 Cut"
  Direction = (0,0,1)
  Length = 100
  Length2 = 10
  Profile = -> Sketch015
  Type = 0
FEATURE [PartDesign::Thickness] Angle002
  Base = -> Pad010 [Face2,Face4,Face3,Face6]
  BaseFeature = -> Pad010
  Intersection = false
  Join = 0
  Mode = 0
  Reversed = true
  SupportTransform = false
  Value = 1
FEATURE [PartDesign::Chamfer] Angle45Cut
  Angle = 45
  Base = -> Angle002 [Edge11,Edge13]
  BaseFeature = -> Angle002
  ChamferType = 0
  FlipDirection = false
  Size = 98.99
  Size2 = 1
  SupportTransform = false
  UseAllEdges = false
FEATURE [PartDesign::Body] Body011  label="Body, Construction003"
  Group = -> [Sketch015,Pad010,Angle002,Angle45Cut]
  Origin = -> Origin015
  Tip = -> Angle45Cut
COMPONENT P20 — recipe-attached ("Part, Frame", modeled in this document).
Construction recipe (the document's own serialized feature program — sketch geometry with constraints, then the solid features built on it; lengths are millimeters unless a unit is written):

FEATURE [Sketcher::SketchObject] Sketch016  label="Pattern, Frame"
  AttachmentOffset = pos=(800,0,1618) rot=(0,0,1;0rad)
  FullyConstrained = true
  MapMode = 5
  Placement = pos=(800,-1618,-3.593e-13) rot=(1,0,0;1.5708rad)
  Support = -> [XZ_Plane017]
  sketch-geometry (4):
    g0: LineSegment StartX=0 StartY=40 StartZ=0 EndX=600 EndY=40 EndZ=0
    g1: LineSegment StartX=600 StartY=40 StartZ=0 EndX=600 EndY=0 EndZ=0
    g2: LineSegment StartX=600 StartY=0 StartZ=0 EndX=0 EndY=0 EndZ=0
    g3: LineSegment StartX=0 StartY=0 StartZ=0 EndX=0 EndY=40 EndZ=0
  constraints (11):
    c: Coincident(g0,g1)
    c: Coincident(g1,g2)
    c: Coincident(g2,g3)
    c: Coincident(g3,g0)
    c: Horizontal(g0)
    c: Horizontal(g2)
    c: Vertical(g1)
    c: Vertical(g3)
    c: Coincident(g2,g-1)
    c: DistanceX(g0,g0) = 600  'SizeX'
    c: DistanceY(g3,g3) = 40  'SizeY'
FEATURE [PartDesign::Pad] Pad011  label="Frame"
  Direction = (0,-1,2e-16)
  Length = 20
  Length2 = 10
  Placement = pos=(0,0,0) rot=(1,0,0;1.5708rad)
  Profile = -> Sketch016
  Type = 0
FEATURE [PartDesign::Chamfer] Frame45Cut
  Angle = 45
  Base = -> Pad011 [Edge1,Edge2]
  BaseFeature = -> Pad011
  ChamferType = 0
  FlipDirection = false
  Placement = pos=(0,0,0) rot=(1,0,0;1.5708rad)
  Size = 39.99
  Size2 = 1
  SupportTransform = false
  UseAllEdges = false
FEATURE [PartDesign::Body] Body012  label="Body, Frame"
  Group = -> [Sketch016,Pad011,Frame45Cut]
  Origin = -> Origin017
  Tip = -> Frame45Cut
COMPONENT P21 — recipe-attached ("Part, Frame001", modeled in this document).
Construction recipe (the document's own serialized feature program — sketch geometry with constraints, then the solid features built on it; lengths are millimeters unless a unit is written):

FEATURE [Sketcher::SketchObject] Sketch017  label="Pattern, Frame001"
  AttachmentOffset = pos=(800,-1938,0) rot=(0,0,1;0rad)
  FullyConstrained = true
  MapMode = 5
  Placement = pos=(800,-1938,0) rot=(0,0,1;0rad)
  Support = -> [XY_Plane019]
  sketch-geometry (4):
    g0: LineSegment StartX=0 StartY=100 StartZ=0 EndX=600 EndY=100 EndZ=0
    g1: LineSegment StartX=600 StartY=100 StartZ=0 EndX=600 EndY=0 EndZ=0
    g2: LineSegment StartX=600 StartY=0 StartZ=0 EndX=0 EndY=0 EndZ=0
    g3: LineSegment StartX=0 StartY=0 StartZ=0 EndX=0 EndY=100 EndZ=0
  constraints (11):
    c: Coincident(g0,g1)
    c: Coincident(g1,g2)
    c: Coincident(g2,g3)
    c: Coincident(g3,g0)
    c: Horizontal(g0)
    c: Horizontal(g2)
    c: Vertical(g1)
    c: Vertical(g3)
    c: Coincident(g2,g-1)
    c: DistanceX(g0,g0) = 600  'SizeX'
    c: DistanceY(g3,g3) = 100  'SizeY'
FEATURE [PartDesign::Pad] Pad012  label="Frame Table Foot"
  Direction = (0,0,1)
  Length = 100
  Length2 = 10
  Profile = -> Sketch017
  Type = 0
FEATURE [PartDesign::Chamfer] Frame45Cut001
  Angle = 45
  Base = -> Pad012 [Edge12,Edge7]
  BaseFeature = -> Pad012
  ChamferType = 0
  FlipDirection = false
  Size = 99.99
  Size2 = 1
  SupportTransform = false
  UseAllEdges = false
FEATURE [Sketcher::SketchObject] routerPattern
  FullyConstrained = true
  Placement = pos=(1300.01,-1888,100) rot=(1,0,0;1.5708rad)
  sketch-geometry (4):
    g0: ArcOfCircle CenterX=49.9999 CenterY=-49.9999 CenterZ=0 NormalX=0 NormalY=0 NormalZ=1 AngleXU=0 Radius=49.9999 StartAngle=1.5708 EndAngle=3.14159
    g1: ArcOfCircle CenterX=-49.9999 CenterY=49.9999 CenterZ=0 NormalX=0 NormalY=0 NormalZ=1 AngleXU=0 Radius=49.9999 StartAngle=4.71239 EndAngle=6.28319
    g2: ArcOfCircle CenterX=49.9999 CenterY=49.9999 CenterZ=0 NormalX=0 NormalY=0 NormalZ=1 AngleXU=0 Radius=49.9999 StartAngle=3.14159 EndAngle=4.71239
    g3: ArcOfCircle CenterX=-49.9999 CenterY=-49.9999 CenterZ=0 NormalX=0 NormalY=0 NormalZ=1 AngleXU=0 Radius=49.9999 StartAngle=6.28318 EndAngle=7.85398
  constraints (16):
    c: Equal(g3,g1)
    c: Equal(g1,g2)
    c: Equal(g2,g0)
    c: Vertical(g0,g2)
    c: Horizontal(g3,g0)
    c: Vertical(g1,g3)
    c: Horizontal(g1,g2)
    c: Coincident(g1,g2)
    c: Coincident(g0,g2)
    c: Coincident(g3,g0)
    c: Coincident(g3,g1)
    c: PointOnObject(g1,g-1)
    c: PointOnObject(g1,g-2)
    c: DistanceY(g0,g-1) = 50
    c: Vertical(g0,g0)
    c: Horizontal(g1,g1)
FEATURE [PartDesign::Pocket] router  label="RoundOver2 "
  BaseFeature = -> Frame45Cut001
  Direction = (0,1,-2e-16)
  Length = 5
  Length2 = 5
  Midplane = true
  Profile = -> routerPattern
  Type = 1
FEATURE [Sketcher::SketchObject] routerPattern001
  FullyConstrained = true
  Placement = pos=(899.99,-1888,100) rot=(1,0,0;1.5708rad)
  sketch-geometry (4):
    g0: ArcOfCircle CenterX=50 CenterY=-50 CenterZ=0 NormalX=0 NormalY=0 NormalZ=1 AngleXU=0 Radius=50 StartAngle=1.5708 EndAngle=3.14159
    g1: ArcOfCircle CenterX=-50 CenterY=50 CenterZ=0 NormalX=0 NormalY=0 NormalZ=1 AngleXU=0 Radius=50 StartAngle=4.71239 EndAngle=6.28319
    g2: ArcOfCircle CenterX=50 CenterY=50 CenterZ=0 NormalX=0 NormalY=0 NormalZ=1 AngleXU=0 Radius=50 StartAngle=3.14159 EndAngle=4.71239
    g3: ArcOfCircle CenterX=-50 CenterY=-50 CenterZ=0 NormalX=0 NormalY=0 NormalZ=1 AngleXU=0 Radius=50 StartAngle=6.28318 EndAngle=7.85398
  constraints (16):
    c: Equal(g3,g1)
    c: Equal(g1,g2)
    c: Equal(g2,g0)
    c: Vertical(g0,g2)
    c: Horizontal(g3,g0)
    c: Vertical(g1,g3)
    c: Horizontal(g1,g2)
    c: Coincident(g1,g2)
    c: Coincident(g0,g2)
    c: Coincident(g3,g0)
    c: Coincident(g3,g1)
    c: PointOnObject(g1,g-1)
    c: PointOnObject(g1,g-2)
    c: DistanceY(g0,g-1) = 50
    c: Vertical(g0,g0)
    c: Horizontal(g1,g1)
FEATURE [PartDesign::Pocket] router001  label="RoundOver2 001"
  BaseFeature = -> router
  Direction = (0,1,-2e-16)
  Length = 5
  Length2 = 5
  Midplane = true
  Profile = -> routerPattern001
  Type = 1
FEATURE [Sketcher::SketchObject] Sketch018
  FullyConstrained = true
  MapMode = 5
  Placement = pos=(1200.01,-1888,100) rot=(0,0,1;0rad)
  sketch-geometry (1):
    g0: Circle CenterX=0 CenterY=0 CenterZ=0 NormalX=0 NormalY=0 NormalZ=1 AngleXU=0 Radius=5
  constraints (2):
    c: Coincident(g0,g-1)
    c: Diameter(g0) = 10  'Hole00Diameter'
FEATURE [PartDesign::Hole] Hole
  BaseFeature = -> router001
  CustomThreadClearance = 0
  Depth = 25
  DepthType = 0
  Diameter = 10
  DrillForDepth = true
  DrillPoint = 1
  DrillPointAngle = 118
  HoleCutCountersinkAngle = 90
  HoleCutCustomValues = false
  HoleCutDepth = 25
  HoleCutDiameter = 10
  HoleCutType = 0
  ModelThread = false
  Profile = -> Sketch018
  Tapered = false
  TaperedAngle = 90
  ThreadClass = 0
  ThreadDepth = 25
  ThreadDepthType = 0
  ThreadDirection = 0
  ThreadFit = 0
  ThreadSize = 0
  ThreadType = 0
  Threaded = false
  UseCustomThreadClearance = false
FEATURE [Sketcher::SketchObject] Sketch019
  FullyConstrained = true
  MapMode = 5
  Placement = pos=(1168.01,-1888,100) rot=(0,0,1;0rad)
  sketch-geometry (1):
    g0: Circle CenterX=0 CenterY=0 CenterZ=0 NormalX=0 NormalY=0 NormalZ=1 AngleXU=0 Radius=5
  constraints (2):
    c: Coincident(g0,g-1)
    c: Diameter(g0) = 10  'Hole00Diameter'
FEATURE [PartDesign::Hole] Hole001
  BaseFeature = -> Hole
  CustomThreadClearance = 0
  Depth = 25
  DepthType = 0
  Diameter = 10
  DrillForDepth = true
  DrillPoint = 1
  DrillPointAngle = 118
  HoleCutCountersinkAngle = 90
  HoleCutCustomValues = false
  HoleCutDepth = 25
  HoleCutDiameter = 10
  HoleCutType = 0
  ModelThread = false
  Profile = -> Sketch019
  Tapered = false
  TaperedAngle = 90
  ThreadClass = 0
  ThreadDepth = 25
  ThreadDepthType = 0
  ThreadDirection = 0
  ThreadFit = 0
  ThreadSize = 0
  ThreadType = 0
  Threaded = false
  UseCustomThreadClearance = false
FEATURE [Sketcher::SketchObject] Sketch020
  FullyConstrained = true
  MapMode = 5
  Placement = pos=(999.99,-1888,100) rot=(0,0,1;0rad)
  sketch-geometry (1):
    g0: Circle CenterX=0 CenterY=0 CenterZ=0 NormalX=0 NormalY=0 NormalZ=1 AngleXU=0 Radius=5
  constraints (2):
    c: Coincident(g0,g-1)
    c: Diameter(g0) = 10  'Hole00Diameter'
FEATURE [PartDesign::Hole] Hole002
  BaseFeature = -> Hole001
  CustomThreadClearance = 0
  Depth = 25
  DepthType = 0
  Diameter = 10
  DrillForDepth = true
  DrillPoint = 1
  DrillPointAngle = 118
  HoleCutCountersinkAngle = 90
  HoleCutCustomValues = false
  HoleCutDepth = 25
  HoleCutDiameter = 10
  HoleCutType = 0
  ModelThread = false
  Profile = -> Sketch020
  Tapered = false
  TaperedAngle = 90
  ThreadClass = 0
  ThreadDepth = 25
  ThreadDepthType = 0
  ThreadDirection = 0
  ThreadFit = 0
  ThreadSize = 0
  ThreadType = 0
  Threaded = false
  UseCustomThreadClearance = false
FEATURE [Sketcher::SketchObject] Sketch021
  FullyConstrained = true
  MapMode = 5
  Placement = pos=(1031.99,-1888,100) rot=(0,0,1;0rad)
  sketch-geometry (1):
    g0: Circle CenterX=0 CenterY=0 CenterZ=0 NormalX=0 NormalY=0 NormalZ=1 AngleXU=0 Radius=5
  constraints (2):
    c: Coincident(g0,g-1)
    c: Diameter(g0) = 10  'Hole00Diameter'
FEATURE [PartDesign::Hole] Hole003
  BaseFeature = -> Hole002
  CustomThreadClearance = 0
  Depth = 25
  DepthType = 0
  Diameter = 10
  DrillForDepth = true
  DrillPoint = 1
  DrillPointAngle = 118
  HoleCutCountersinkAngle = 90
  HoleCutCustomValues = false
  HoleCutDepth = 25
  HoleCutDiameter = 10
  HoleCutType = 0
  ModelThread = false
  Profile = -> Sketch021
  Tapered = false
  TaperedAngle = 90
  ThreadClass = 0
  ThreadDepth = 25
  ThreadDepthType = 0
  ThreadDirection = 0
  ThreadFit = 0
  ThreadSize = 0
  ThreadType = 0
  Threaded = false
  UseCustomThreadClearance = false
FEATURE [PartDesign::Body] Body013  label="Body, Frame001"
  Group = -> [Sketch017,Pad012,Frame45Cut001,routerPattern,router,routerPattern001,router001,Sketch018,Hole,Sketch019,Hole001,Sketch020,Hole002,Sketch021,Hole003]
  Origin = -> Origin019
  Tip = -> Hole003
COMPONENT P22 — recipe-attached ("Part, Holes", modeled in this document).
Construction recipe (the document's own serialized feature program — sketch geometry with constraints, then the solid features built on it; lengths are millimeters unless a unit is written):

FEATURE [Sketcher::SketchObject] Sketch022  label="Pattern, panel with dowels"
  AttachmentOffset = pos=(-918,0,2250) rot=(0,0,1;0rad)
  FullyConstrained = true
  MapMode = 5
  Placement = pos=(-918,-2250,-4.996e-13) rot=(1,0,0;1.5708rad)
  Support = -> [XZ_Plane021]
  sketch-geometry (4):
    g0: LineSegment StartX=0 StartY=300 StartZ=0 EndX=600 EndY=300 EndZ=0
    g1: LineSegment StartX=600 StartY=300 StartZ=0 EndX=600 EndY=0 EndZ=0
    g2: LineSegment StartX=600 StartY=0 StartZ=0 EndX=0 EndY=0 EndZ=0
    g3: LineSegment StartX=0 StartY=0 StartZ=0 EndX=0 EndY=300 EndZ=0
  constraints (11):
    c: Coincident(g0,g1)
    c: Coincident(g1,g2)
    c: Coincident(g2,g3)
    c: Coincident(g3,g0)
    c: Horizontal(g0)
    c: Horizontal(g2)
    c: Vertical(g1)
    c: Vertical(g3)
    c: Coincident(g2,g-1)
    c: DistanceX(g0,g0) = 600  'SizeX'
    c: DistanceY(g3,g3) = 300  'SizeY'
FEATURE [PartDesign::Pad] Pad013  label="panel with holes"
  Direction = (0,-1,2e-16)
  Length = 18
  Length2 = 10
  Placement = pos=(0,0,0) rot=(1,0,0;1.5708rad)
  Profile = -> Sketch022
  Type = 0
FEATURE [Sketcher::SketchObject] Sketch023
  FullyConstrained = true
  MapMode = 5
  Placement = pos=(-368,-2259,300) rot=(0,0,1;0rad)
  sketch-geometry (1):
    g0: Circle CenterX=0 CenterY=0 CenterZ=0 NormalX=0 NormalY=0 NormalZ=1 AngleXU=0 Radius=4
  constraints (2):
    c: Coincident(g0,g-1)
    c: Diameter(g0) = 8  'Hole00Diameter'
FEATURE [PartDesign::Hole] Hole004
  BaseFeature = -> Pad013
  CustomThreadClearance = 0
  Depth = 35
  DepthType = 0
  Diameter = 8
  DrillForDepth = true
  DrillPoint = 1
  DrillPointAngle = 118
  HoleCutCountersinkAngle = 90
  HoleCutCustomValues = false
  HoleCutDepth = 35
  HoleCutDiameter = 8
  HoleCutType = 0
  ModelThread = false
  Placement = pos=(0,0,0) rot=(1,0,0;1.5708rad)
  Profile = -> Sketch023
  Tapered = false
  TaperedAngle = 90
  ThreadClass = 0
  ThreadDepth = 35
  ThreadDepthType = 0
  ThreadDirection = 0
  ThreadFit = 0
  ThreadSize = 0
  ThreadType = 0
  Threaded = false
  UseCustomThreadClearance = false
FEATURE [Sketcher::SketchObject] Sketch024
  FullyConstrained = true
  MapMode = 5
  Placement = pos=(-400,-2259,300) rot=(0,0,1;0rad)
  sketch-geometry (1):
    g0: Circle CenterX=0 CenterY=0 CenterZ=0 NormalX=0 NormalY=0 NormalZ=1 AngleXU=0 Radius=4
  constraints (2):
    c: Coincident(g0,g-1)
    c: Diameter(g0) = 8  'Hole00Diameter'
FEATURE [PartDesign::Hole] Hole005
  BaseFeature = -> Hole004
  CustomThreadClearance = 0
  Depth = 35
  DepthType = 0
  Diameter = 8
  DrillForDepth = true
  DrillPoint = 1
  DrillPointAngle = 118
  HoleCutCountersinkAngle = 90
  HoleCutCustomValues = false
  HoleCutDepth = 35
  HoleCutDiameter = 8
  HoleCutType = 0
  ModelThread = false
  Placement = pos=(0,0,0) rot=(1,0,0;1.5708rad)
  Profile = -> Sketch024
  Tapered = false
  TaperedAngle = 90
  ThreadClass = 0
  ThreadDepth = 35
  ThreadDepthType = 0
  ThreadDirection = 0
  ThreadFit = 0
  ThreadSize = 0
  ThreadType = 0
  Threaded = false
  UseCustomThreadClearance = false
FEATURE [Sketcher::SketchObject] Sketch025
  FullyConstrained = true
  MapMode = 5
  Placement = pos=(-868,-2259,300) rot=(0,0,1;0rad)
  sketch-geometry (1):
    g0: Circle CenterX=0 CenterY=0 CenterZ=0 NormalX=0 NormalY=0 NormalZ=1 AngleXU=0 Radius=4
  constraints (2):
    c: Coincident(g0,g-1)
    c: Diameter(g0) = 8  'Hole00Diameter'
FEATURE [PartDesign::Hole] Hole006
  BaseFeature = -> Hole005
  CustomThreadClearance = 0
  Depth = 35
  DepthType = 0
  Diameter = 8
  DrillForDepth = true
  DrillPoint = 1
  DrillPointAngle = 118
  HoleCutCountersinkAngle = 90
  HoleCutCustomValues = false
  HoleCutDepth = 35
  HoleCutDiameter = 8
  HoleCutType = 0
  ModelThread = false
  Placement = pos=(0,0,0) rot=(1,0,0;1.5708rad)
  Profile = -> Sketch025
  Tapered = false
  TaperedAngle = 90
  ThreadClass = 0
  ThreadDepth = 35
  ThreadDepthType = 0
  ThreadDirection = 0
  ThreadFit = 0
  ThreadSize = 0
  ThreadType = 0
  Threaded = false
  UseCustomThreadClearance = false
FEATURE [Sketcher::SketchObject] Sketch026
  FullyConstrained = true
  MapMode = 5
  Placement = pos=(-836,-2259,300) rot=(0,0,1;0rad)
  sketch-geometry (1):
    g0: Circle CenterX=0 CenterY=0 CenterZ=0 NormalX=0 NormalY=0 NormalZ=1 AngleXU=0 Radius=4
  constraints (2):
    c: Coincident(g0,g-1)
    c: Diameter(g0) = 8  'Hole00Diameter'
FEATURE [PartDesign::Hole] Hole007
  BaseFeature = -> Hole006
  CustomThreadClearance = 0
  Depth = 35
  DepthType = 0
  Diameter = 8
  DrillForDepth = true
  DrillPoint = 1
  DrillPointAngle = 118
  HoleCutCountersinkAngle = 90
  HoleCutCustomValues = false
  HoleCutDepth = 35
  HoleCutDiameter = 8
  HoleCutType = 0
  ModelThread = false
  Placement = pos=(0,0,0) rot=(1,0,0;1.5708rad)
  Profile = -> Sketch026
  Tapered = false
  TaperedAngle = 90
  ThreadClass = 0
  ThreadDepth = 35
  ThreadDepthType = 0
  ThreadDirection = 0
  ThreadFit = 0
  ThreadSize = 0
  ThreadType = 0
  Threaded = false
  UseCustomThreadClearance = false
FEATURE [Sketcher::SketchObject] Sketch027
  FullyConstrained = true
  MapMode = 5
  Placement = pos=(-327,-2268,250) rot=(1,0,0;1.5708rad)
  sketch-geometry (2):
    g0: Circle CenterX=0 CenterY=0 CenterZ=0 NormalX=0 NormalY=0 NormalZ=1 AngleXU=0 Radius=1.5
    g1: Circle CenterX=0 CenterY=0 CenterZ=0 NormalX=0 NormalY=0 NormalZ=1 AngleXU=0 Radius=5
  constraints (4):
    c: Coincident(g0,g-1)
    c: Diameter(g0) = 3  'Hole00Diameter'
    c: Coincident(g1,g-1)
    c: Diameter(g1) = 10  'Countersink00Diameter'
FEATURE [PartDesign::Hole] Countersink
  BaseFeature = -> Hole007
  CustomThreadClearance = 0
  Depth = 40
  DepthType = 0
  Diameter = 3
  DrillForDepth = true
  DrillPoint = 1
  DrillPointAngle = 118
  HoleCutCountersinkAngle = 90
  HoleCutCustomValues = false
  HoleCutDepth = 5
  HoleCutDiameter = 10
  HoleCutType = 2
  ModelThread = false
  Placement = pos=(0,0,0) rot=(1,0,0;1.5708rad)
  Profile = -> Sketch027
  Tapered = false
  TaperedAngle = 90
  ThreadClass = 0
  ThreadDepth = 40
  ThreadDepthType = 0
  ThreadDirection = 0
  ThreadFit = 0
  ThreadSize = 0
  ThreadType = 0
  Threaded = false
  UseCustomThreadClearance = false
FEATURE [Sketcher::SketchObject] Sketch028
  FullyConstrained = true
  MapMode = 5
  Placement = pos=(-327,-2268,50) rot=(1,0,0;1.5708rad)
  sketch-geometry (2):
    g0: Circle CenterX=0 CenterY=0 CenterZ=0 NormalX=0 NormalY=0 NormalZ=1 AngleXU=0 Radius=1.5
    g1: Circle CenterX=0 CenterY=0 CenterZ=0 NormalX=0 NormalY=0 NormalZ=1 AngleXU=0 Radius=5
  constraints (4):
    c: Coincident(g0,g-1)
    c: Diameter(g0) = 3  'Hole00Diameter'
    c: Coincident(g1,g-1)
    c: Diameter(g1) = 10  'Countersink00Diameter'
FEATURE [PartDesign::Hole] Countersink001
  BaseFeature = -> Countersink
  CustomThreadClearance = 0
  Depth = 40
  DepthType = 0
  Diameter = 3
  DrillForDepth = true
  DrillPoint = 1
  DrillPointAngle = 118
  HoleCutCountersinkAngle = 90
  HoleCutCustomValues = false
  HoleCutDepth = 5
  HoleCutDiameter = 10
  HoleCutType = 2
  ModelThread = false
  Placement = pos=(0,0,0) rot=(1,0,0;1.5708rad)
  Profile = -> Sketch028
  Tapered = false
  TaperedAngle = 90
  ThreadClass = 0
  ThreadDepth = 40
  ThreadDepthType = 0
  ThreadDirection = 0
  ThreadFit = 0
  ThreadSize = 0
  ThreadType = 0
  Threaded = false
  UseCustomThreadClearance = false
FEATURE [Sketcher::SketchObject] Sketch029
  FullyConstrained = true
  MapMode = 5
  Placement = pos=(-858,-2274,250) rot=(0.677661,0.519988,0.519988;1.95044rad)
  sketch-geometry (2):
    g0: Circle CenterX=0 CenterY=0 CenterZ=0 NormalX=0 NormalY=0 NormalZ=1 AngleXU=0 Radius=1.5
    g1: Circle CenterX=0 CenterY=0 CenterZ=0 NormalX=0 NormalY=0 NormalZ=1 AngleXU=0 Radius=4.75
  constraints (4):
    c: Coincident(g0,g-1)
    c: Diameter(g0) = 3  'Tip0hole00Diameter'
    c: Coincident(g1,g-1)
    c: Diameter(g1) = 9.5  'Pocket0hole00Diameter'
FEATURE [PartDesign::Hole] PocketHole
  BaseFeature = -> Countersink001
  CustomThreadClearance = 0
  Depth = 90
  DepthType = 0
  Diameter = 3
  DrillForDepth = false
  DrillPoint = 0
  DrillPointAngle = 118
  HoleCutCountersinkAngle = 90
  HoleCutCustomValues = false
  HoleCutDepth = 45
  HoleCutDiameter = 9.5
  HoleCutType = 1
  ModelThread = false
  Placement = pos=(0,0,0) rot=(1,0,0;1.5708rad)
  Profile = -> Sketch029
  Tapered = false
  TaperedAngle = 90
  ThreadClass = 0
  ThreadDepth = 90
  ThreadDepthType = 0
  ThreadDirection = 0
  ThreadFit = 0
  ThreadSize = 0
  ThreadType = 0
  Threaded = false
  UseCustomThreadClearance = false
FEATURE [Sketcher::SketchObject] Sketch030
  FullyConstrained = true
  MapMode = 5
  Placement = pos=(-858,-2274,218) rot=(0.677661,0.519988,0.519988;1.95044rad)
  sketch-geometry (2):
    g0: Circle CenterX=0 CenterY=0 CenterZ=0 NormalX=0 NormalY=0 NormalZ=1 AngleXU=0 Radius=1.5
    g1: Circle CenterX=0 CenterY=0 CenterZ=0 NormalX=0 NormalY=0 NormalZ=1 AngleXU=0 Radius=4.75
  constraints (4):
    c: Coincident(g0,g-1)
    c: Diameter(g0) = 3  'Tip0hole00Diameter'
    c: Coincident(g1,g-1)
    c: Diameter(g1) = 9.5  'Pocket0hole00Diameter'
FEATURE [PartDesign::Hole] PocketHole001
  BaseFeature = -> PocketHole
  CustomThreadClearance = 0
  Depth = 90
  DepthType = 0
  Diameter = 3
  DrillForDepth = false
  DrillPoint = 0
  DrillPointAngle = 118
  HoleCutCountersinkAngle = 90
  HoleCutCustomValues = false
  HoleCutDepth = 45
  HoleCutDiameter = 9.5
  HoleCutType = 1
  ModelThread = false
  Placement = pos=(0,0,0) rot=(1,0,0;1.5708rad)
  Profile = -> Sketch030
  Tapered = false
  TaperedAngle = 90
  ThreadClass = 0
  ThreadDepth = 90
  ThreadDepthType = 0
  ThreadDirection = 0
  ThreadFit = 0
  ThreadSize = 0
  ThreadType = 0
  Threaded = false
  UseCustomThreadClearance = false
FEATURE [Sketcher::SketchObject] Sketch031
  FullyConstrained = true
  MapMode = 5
  Placement = pos=(-858,-2274,50) rot=(0.677661,0.519988,0.519988;1.95044rad)
  sketch-geometry (2):
    g0: Circle CenterX=0 CenterY=0 CenterZ=0 NormalX=0 NormalY=0 NormalZ=1 AngleXU=0 Radius=1.5
    g1: Circle CenterX=0 CenterY=0 CenterZ=0 NormalX=0 NormalY=0 NormalZ=1 AngleXU=0 Radius=4.75
  constraints (4):
    c: Coincident(g0,g-1)
    c: Diameter(g0) = 3  'Tip0hole00Diameter'
    c: Coincident(g1,g-1)
    c: Diameter(g1) = 9.5  'Pocket0hole00Diameter'
FEATURE [PartDesign::Hole] PocketHole002
  BaseFeature = -> PocketHole001
  CustomThreadClearance = 0
  Depth = 90
  DepthType = 0
  Diameter = 3
  DrillForDepth = false
  DrillPoint = 0
  DrillPointAngle = 118
  HoleCutCountersinkAngle = 90
  HoleCutCustomValues = false
  HoleCutDepth = 45
  HoleCutDiameter = 9.5
  HoleCutType = 1
  ModelThread = false
  Placement = pos=(0,0,0) rot=(1,0,0;1.5708rad)
  Profile = -> Sketch031
  Tapered = false
  TaperedAngle = 90
  ThreadClass = 0
  ThreadDepth = 90
  ThreadDepthType = 0
  ThreadDirection = 0
  ThreadFit = 0
  ThreadSize = 0
  ThreadType = 0
  Threaded = false
  UseCustomThreadClearance = false
FEATURE [Sketcher::SketchObject] Sketch032
  FullyConstrained = true
  MapMode = 5
  Placement = pos=(-858,-2274,82) rot=(0.677661,0.519988,0.519988;1.95044rad)
  sketch-geometry (2):
    g0: Circle CenterX=0 CenterY=0 CenterZ=0 NormalX=0 NormalY=0 NormalZ=1 AngleXU=0 Radius=1.5
    g1: Circle CenterX=0 CenterY=0 CenterZ=0 NormalX=0 NormalY=0 NormalZ=1 AngleXU=0 Radius=4.75
  constraints (4):
    c: Coincident(g0,g-1)
    c: Diameter(g0) = 3  'Tip0hole00Diameter'
    c: Coincident(g1,g-1)
    c: Diameter(g1) = 9.5  'Pocket0hole00Diameter'
FEATURE [PartDesign::Hole] PocketHole003
  BaseFeature = -> PocketHole002
  CustomThreadClearance = 0
  Depth = 90
  DepthType = 0
  Diameter = 3
  DrillForDepth = false
  DrillPoint = 0
  DrillPointAngle = 118
  HoleCutCountersinkAngle = 90
  HoleCutCustomValues = false
  HoleCutDepth = 45
  HoleCutDiameter = 9.5
  HoleCutType = 1
  ModelThread = false
  Placement = pos=(0,0,0) rot=(1,0,0;1.5708rad)
  Profile = -> Sketch032
  Tapered = false
  TaperedAngle = 90
  ThreadClass = 0
  ThreadDepth = 90
  ThreadDepthType = 0
  ThreadDirection = 0
  ThreadFit = 0
  ThreadSize = 0
  ThreadType = 0
  Threaded = false
  UseCustomThreadClearance = false
FEATURE [PartDesign::Body] Body014  label="Body, Holes"
  Group = -> [Sketch022,Pad013,Sketch023,Hole004,Sketch024,Hole005,Sketch025,Hole006,Sketch026,Hole007,Sketch027,Countersink,Sketch028,Countersink001,Sketch029,PocketHole,Sketch030,PocketHole001,Sketch031,PocketHole002,Sketch032,PocketHole003]
  Origin = -> Origin021
  Tip = -> PocketHole003
COMPONENT P23 — recipe-attached ("Part, panel2pad", modeled in this document).
Construction recipe (the document's own serialized feature program — sketch geometry with constraints, then the solid features built on it; lengths are millimeters unless a unit is written):

FEATURE [Sketcher::SketchObject] Sketch033  label="Pattern, panel2pad"
  AttachmentOffset = pos=(2502,0,1582) rot=(0,0,1;0rad)
  FullyConstrained = true
  MapMode = 5
  Placement = pos=(2502,-1582,-3.513e-13) rot=(1,0,0;1.5708rad)
  Support = -> [XZ_Plane023]
  sketch-geometry (4):
    g0: LineSegment StartX=0 StartY=300 StartZ=0 EndX=600 EndY=300 EndZ=0
    g1: LineSegment StartX=600 StartY=300 StartZ=0 EndX=600 EndY=0 EndZ=0
    g2: LineSegment StartX=600 StartY=0 StartZ=0 EndX=0 EndY=0 EndZ=0
    g3: LineSegment StartX=0 StartY=0 StartZ=0 EndX=0 EndY=300 EndZ=0
  constraints (11):
    c: Coincident(g0,g1)
    c: Coincident(g1,g2)
    c: Coincident(g2,g3)
    c: Coincident(g3,g0)
    c: Horizontal(g0)
    c: Horizontal(g2)
    c: Vertical(g1)
    c: Vertical(g3)
    c: Coincident(g2,g-1)
    c: DistanceX(g0,g0) = 600  'SizeX'
    c: DistanceY(g3,g3) = 300  'SizeY'
FEATURE [PartDesign::Pad] Pad014  label="panel Mortise and Tenon"
  Direction = (0,-1,2e-16)
  Length = 18
  Length2 = 10
  Placement = pos=(0,0,0) rot=(1,0,0;1.5708rad)
  Profile = -> Sketch033
  Type = 0
FEATURE [Sketcher::SketchObject] Sketch034  label="Joint Pattern"
  FullyConstrained = true
  MapMode = 5
  Placement = pos=(0,1.32e-13,300) rot=(0,0,1;3.14159rad)
  Support = -> [Pad014]
  sketch-geometry (4):
    g0: ArcOfCircle CenterX=0 CenterY=-7 CenterZ=0 NormalX=0 NormalY=0 NormalZ=1 AngleXU=0 Radius=3 StartAngle=3.14159 EndAngle=6.28319
    g1: ArcOfCircle CenterX=0 CenterY=7 CenterZ=0 NormalX=0 NormalY=0 NormalZ=1 AngleXU=0 Radius=3 StartAngle=1e-16 EndAngle=3.14159
    g2: LineSegment StartX=3 StartY=-7 StartZ=0 EndX=3 EndY=7 EndZ=0
    g3: LineSegment StartX=-3 StartY=7 StartZ=0 EndX=-3 EndY=-7 EndZ=0
  constraints (9):
    c: Tangent(g0,g2) = -1.5708
    c: Tangent(g2,g1) = -1.5708
    c: Tangent(g1,g3) = -1.5708
    c: Tangent(g3,g0) = -1.5708
    c: Equal(g0,g1)
    c: PointOnObject(g1,g-2)
    c: Symmetric(g1,g0,g-1)
    c: DistanceY(g3,g3) = 14
    c: Radius(g1) = 3
FEATURE [Part::Part2DObjectPython] Clone2D001  label="Pattern from Joint Pattern 001"  # Draft 2D object (typed FeaturePython)
  Fuse = false
  Objects = -> [Sketch034]
  Placement = pos=(2552,-1591,300) rot=(0,0,1;1.5708rad)
  Scale = (1,1,1)
FEATURE [PartDesign::Pad] Tenon  label="Tenon "
  BaseFeature = -> Pad014
  Direction = (0,0,1)
  Length = 30
  Length2 = 10
  Midplane = true
  Placement = pos=(0,0,0) rot=(1,0,0;1.5708rad)
  Profile = -> Clone2D001
  Type = 0
FEATURE [Part::Part2DObjectPython] Clone2D002  label="Pattern from Joint Pattern 002"  # Draft 2D object (typed FeaturePython)
  Fuse = false
  Objects = -> [Sketch034]
  Placement = pos=(2584,-1591,300) rot=(0,0,1;1.5708rad)
  Scale = (1,1,1)
FEATURE [PartDesign::Pad] Tenon001  label="Tenon 001"
  BaseFeature = -> Tenon
  Direction = (0,0,1)
  Length = 30
  Length2 = 10
  Midplane = true
  Placement = pos=(0,0,0) rot=(1,0,0;1.5708rad)
  Profile = -> Clone2D002
  Type = 0
FEATURE [Part::Part2DObjectPython] Clone2D003  label="Pattern from Joint Pattern 003"  # Draft 2D object (typed FeaturePython)
  Fuse = false
  Objects = -> [Sketch034]
  Placement = pos=(3020,-1591,300) rot=(0,0,1;1.5708rad)
  Scale = (1,1,1)
FEATURE [PartDesign::Pad] Tenon002  label="Tenon 002"
  BaseFeature = -> Tenon001
  Direction = (0,0,1)
  Length = 30
  Length2 = 10
  Midplane = true
  Placement = pos=(0,0,0) rot=(1,0,0;1.5708rad)
  Profile = -> Clone2D003
  Type = 0
FEATURE [Part::Part2DObjectPython] Clone2D004  label="Pattern from Joint Pattern 004"  # Draft 2D object (typed FeaturePython)
  Fuse = false
  Objects = -> [Sketch034]
  Placement = pos=(2988,-1591,300) rot=(0,0,1;1.5708rad)
  Scale = (1,1,1)
FEATURE [PartDesign::Pad] Tenon003  label="Tenon 003"
  BaseFeature = -> Tenon002
  Direction = (0,0,1)
  Length = 30
  Length2 = 10
  Midplane = true
  Placement = pos=(0,0,0) rot=(1,0,0;1.5708rad)
  Profile = -> Clone2D004
  Type = 0
FEATURE [Part::Part2DObjectPython] Clone2D005  label="Pattern from Joint Pattern 005"  # Draft 2D object (typed FeaturePython)
  Fuse = false
  Objects = -> [Sketch034]
  Placement = pos=(3093,-1600,250) rot=(0,0.707107,0.707107;3.14159rad)
  Scale = (1,1,1)
FEATURE [PartDesign::Pocket] Mortise  label="Mortise "
  BaseFeature = -> Tenon003
  Direction = (0,-1,2e-16)
  Length = 30
  Length2 = 5
  Midplane = true
  Placement = pos=(0,0,0) rot=(1,0,0;1.5708rad)
  Profile = -> Clone2D005
  Type = 0
FEATURE [Part::Part2DObjectPython] Clone2D006  label="Pattern from Joint Pattern 006"  # Draft 2D object (typed FeaturePython)
  Fuse = false
  Objects = -> [Sketch034]
  Placement = pos=(3093,-1600,218) rot=(0,0.707107,0.707107;3.14159rad)
  Scale = (1,1,1)
FEATURE [PartDesign::Pocket] Mortise001  label="Mortise 001"
  BaseFeature = -> Mortise
  Direction = (0,-1,2e-16)
  Length = 30
  Length2 = 5
  Midplane = true
  Placement = pos=(0,0,0) rot=(1,0,0;1.5708rad)
  Profile = -> Clone2D006
  Type = 0
FEATURE [Part::Part2DObjectPython] Clone2D007  label="Pattern from Joint Pattern 007"  # Draft 2D object (typed FeaturePython)
  Fuse = false
  Objects = -> [Sketch034]
  Placement = pos=(3093,-1600,82) rot=(0,0.707107,0.707107;3.14159rad)
  Scale = (1,1,1)
FEATURE [PartDesign::Pocket] Mortise002  label="Mortise 002"
  BaseFeature = -> Mortise001
  Direction = (0,-1,2e-16)
  Length = 30
  Length2 = 5
  Midplane = true
  Placement = pos=(0,0,0) rot=(1,0,0;1.5708rad)
  Profile = -> Clone2D007
  Type = 0
FEATURE [Part::Part2DObjectPython] Clone2D008  label="Pattern from Joint Pattern 008"  # Draft 2D object (typed FeaturePython)
  Fuse = false
  Objects = -> [Sketch034]
  Placement = pos=(3093,-1600,50) rot=(0,0.707107,0.707107;3.14159rad)
  Scale = (1,1,1)
FEATURE [PartDesign::Pocket] Mortise003  label="Mortise 003"
  BaseFeature = -> Mortise002
  Direction = (0,-1,2e-16)
  Length = 30
  Length2 = 5
  Midplane = true
  Placement = pos=(0,0,0) rot=(1,0,0;1.5708rad)
  Profile = -> Clone2D008
  Type = 0
FEATURE [PartDesign::Body] Body015  label="Body, panel2pad"
  Group = -> [Sketch033,Pad014,Sketch034,Clone2D001,Tenon,Clone2D002,Tenon001,Clone2D003,Tenon002,Clone2D004,Tenon003,Clone2D005,Mortise,Clone2D006,Mortise001,Clone2D007,Mortise002,Clone2D008,Mortise003]
  Origin = -> Origin023
  Tip = -> Mortise003
COMPONENT P24 — geometry summary ("Part009"; no construction recipe available for this part):
  bounding box: 790.4 x 630.7 x 100.0 mm
  tessellated surface: 12 triangles
  volume: 13698095 mm^3 (27% of its bounding box)
  symmetry: 2-fold rotationally symmetric about the z axis; mirror-symmetric across its z mid-plane
PROVENANCE & LICENSES
A FreeCAD (.FCStd) document from a public repository crawl; recipes are the document's own serialized feature recipes (and, for linked parts, companion documents' recipes).
License: mit.
